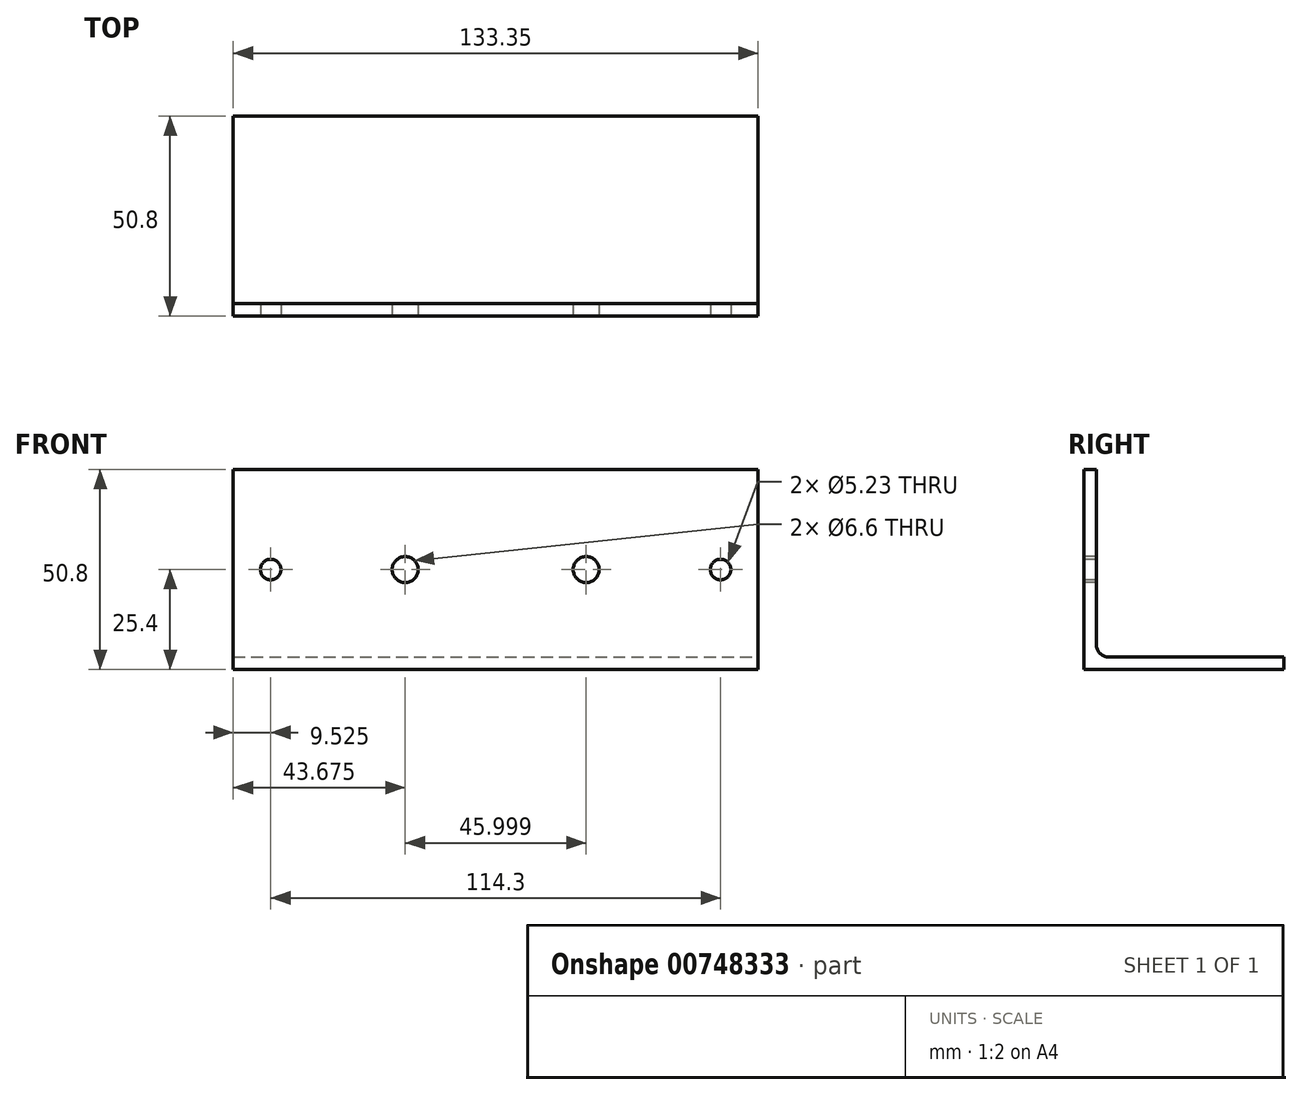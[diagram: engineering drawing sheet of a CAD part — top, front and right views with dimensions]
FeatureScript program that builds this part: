
annotation { "Feature Type Name" : "Feature", "Feature Type Description" : "" }
export const myFeature = defineFeature(function(context is Context, id is Id, definition is map)
    precondition{}
    {
        {
            var Q0;
            Q0=qCreatedBy(makeId("Right.planeOp"),FACE);
            var sketch = newSketch(context, id + "F0", { "sketchPlane" : qUnion([Q0])});
            skLineSegment(sketch, "E0", {"start": v(0, 0) * mm, "end": v(0, -44.45) * mm});
            skLineSegment(sketch, "E1", {"start": v(3.18, -47.62) * mm, "end": v(47.63, -47.62) * mm});
            skLineSegment(sketch, "E2.0", {"start": v(-3.18, -50.8) * mm, "end": v(47.63, -50.8) * mm});
            skLineSegment(sketch, "E2.1", {"start": v(-3.17, 0) * mm, "end": v(-3.18, -50.8) * mm});
            skLineSegment(sketch, "E3", {"start": v(-3.18, 0) * mm, "end": v(0, 0) * mm});
            skLineSegment(sketch, "E4", {"start": v(47.63, -47.62) * mm, "end": v(47.63, -50.8) * mm});
            skPoint(sketch, "E5.visualSharp", {"position": v(0, -47.63) * mm});
            skArc(sketch, "E5.filletArc", {"start": v(0, -44.45) * mm, "mid": v(0.93, -46.7) * mm, "end": v(3.18, -47.63) * mm});
            skSolve(sketch);
        }
        {
            var Q0;
            Q0=makeQuery(id+"F0.imprint","IMPRINT",FACE,{"disambiguationData":[TD([[makeQuery(id+"F0.imprint","IMPRINT",EDGE,{"derivedFrom":sQuery(id+"F0.wireOp",EDGE,"E0")}),-1.0]])]});
            extrude(context, id + "F1", {"entities" : qUnion([Q0]), "oppositeDirection" : true, "depth" : 133.35 * mm, "offsetDistance" : 25.4 * mm});
        }
        {
            var Q0;
            Q0=makeQuery(id+"F1.opExtrude","SWEPT_FACE",FACE,{"disambiguationData":[OSD([sQuery(id+"F0.wireOp",EDGE,"E2.1")])]});
            var sketch = newSketch(context, id + "F2", { "sketchPlane" : qUnion([Q0])});
            skLineSegment(sketch, "E6", {"start": v(0, -25.4) * mm, "end": v(-133.35, -25.4) * mm, "construction": true});
            skLineSegment(sketch, "E7", {"start": v(-66.68, 0) * mm, "end": v(-66.68, -50.8) * mm, "construction": true});
            skLineSegment(sketch, "E8.0", {"start": v(-123.83, 0) * mm, "end": v(-123.83, -50.8) * mm, "construction": true});
            skLineSegment(sketch, "E9.0", {"start": v(-9.53, 0) * mm, "end": v(-9.53, -50.8) * mm, "construction": true});
            skCircle(sketch, "E10", {"center": v(-123.83, -25.4) * mm, "radius": 2.62 * mm});
            skCircle(sketch, "E11", {"center": v(-9.53, -25.4) * mm, "radius": 2.62 * mm});
            skLineSegment(sketch, "E12.bottom", {"start": v(-43.68, -18.9) * mm, "end": v(-89.67, -18.9) * mm, "construction": true});
            skLineSegment(sketch, "E12.top", {"start": v(-43.68, -31.9) * mm, "end": v(-89.67, -31.9) * mm, "construction": true});
            skLineSegment(sketch, "E12.left", {"start": v(-43.68, -18.9) * mm, "end": v(-43.68, -31.9) * mm, "construction": true});
            skLineSegment(sketch, "E12.right", {"start": v(-89.67, -18.9) * mm, "end": v(-89.67, -31.9) * mm, "construction": true});
            skPoint(sketch, "E12.middle", {"position": v(-66.67, -25.4) * mm});
            skCircle(sketch, "E13", {"center": v(-89.67, -25.4) * mm, "radius": 3.3 * mm});
            skCircle(sketch, "E14", {"center": v(-43.68, -25.4) * mm, "radius": 3.3 * mm});
            skSolve(sketch);
        }
        {
            var Q0;
            Q0=qSketchRegion(id+"F2",true);
            extrude(context, id + "F3", {"entities" : qUnion([Q0]), "operationType" : NewBodyOperationType.REMOVE, "endBound" : BoundingType.THROUGH_ALL, "oppositeDirection" : true, "depth" : 25.4 * mm, "offsetDistance" : 25.4 * mm});
        }
    });
